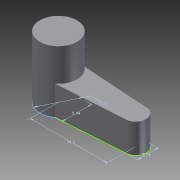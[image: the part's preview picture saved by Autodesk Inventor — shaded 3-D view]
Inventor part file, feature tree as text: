
AUTODESK INVENTOR PART (.ipt)
format: ipt  version: 2011 SP2 (Build 150309200, 309)  size: 80,896 bytes
history: native  units: mm
features: extrude x2, sketch x1
ambient origin geometry x8: Origin, YZ Plane, XZ Plane, XY Plane, X Axis, Y Axis, Z Axis, Center Point
bodies: Solid1 (feature_tree)
feature tree (3):
  sketch  "Sketch1"  dims[d0=6.88mm d1=3.91mm d2=14.2mm d3=5.44mm d4=3.74mm d5=5.384mm d6=0.0mm d7=11.384mm d8=0.0mm]
  extrude  "Extrusion1"  Depth=3.91mm
  extrude  "Extrusion2"  Depth=5.44mm
